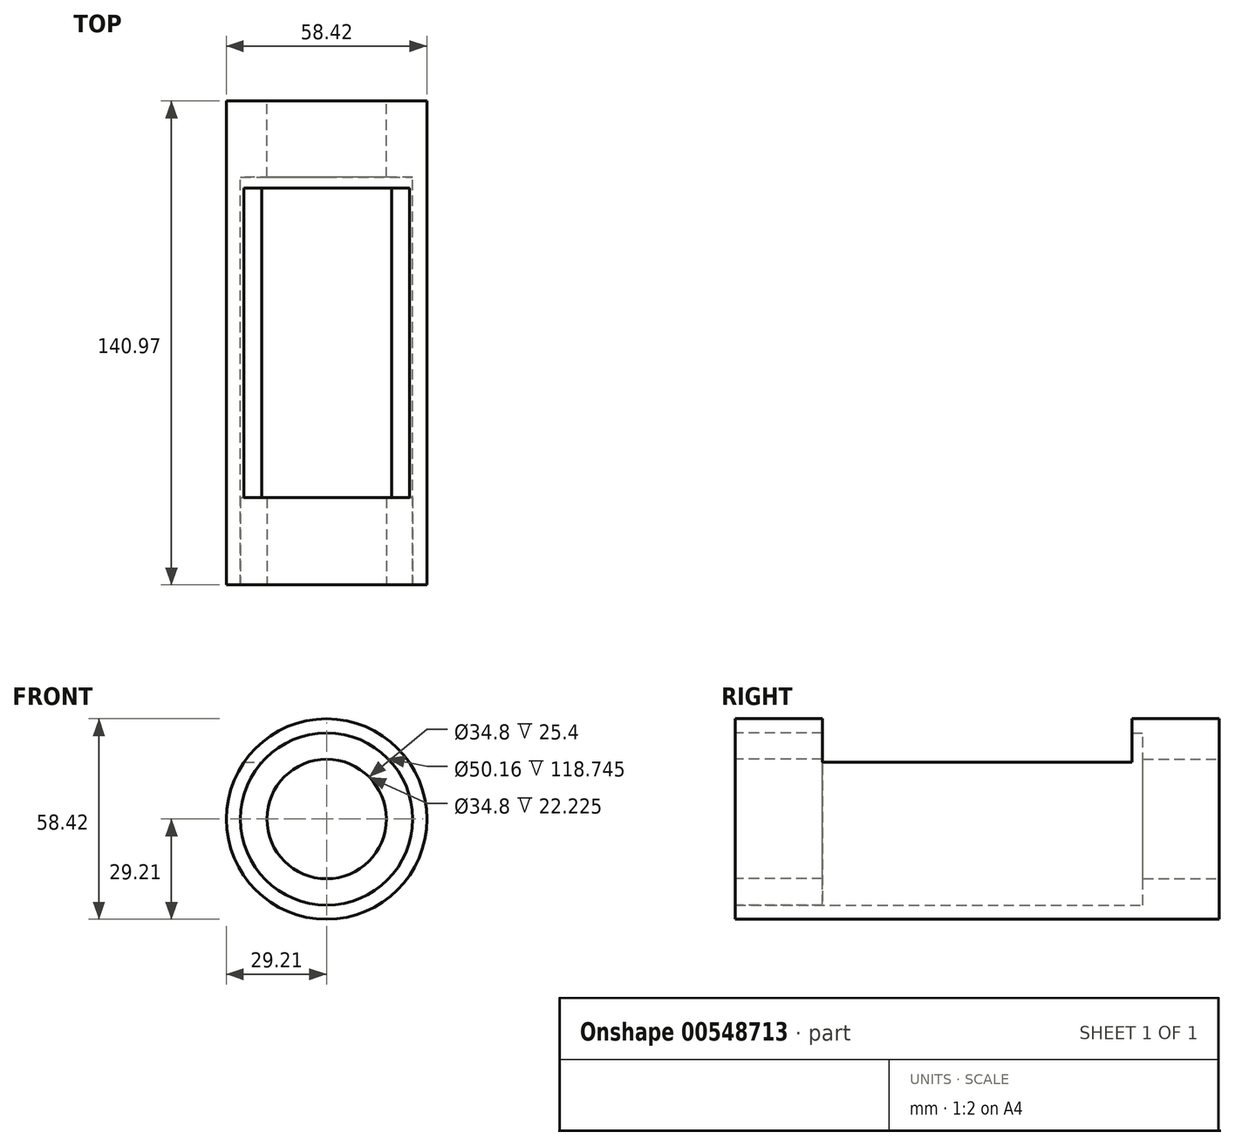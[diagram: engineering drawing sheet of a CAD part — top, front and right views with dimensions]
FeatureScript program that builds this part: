
annotation { "Feature Type Name" : "Feature", "Feature Type Description" : "" }
export const myFeature = defineFeature(function(context is Context, id is Id, definition is map)
    precondition{}
    {
        {
            var Q0;
            Q0=qCreatedBy(makeId("Front.planeOp"),FACE);
            var sketch = newSketch(context, id + "F0", { "sketchPlane" : qUnion([Q0])});
            skCircle(sketch, "E0", {"center": v(0, 0) * mm, "radius": 29.21 * mm});
            skCircle(sketch, "E1", {"center": v(0, 0) * mm, "radius": 25.08 * mm});
            skCircle(sketch, "E2", {"center": v(0, 0) * mm, "radius": 17.4 * mm});
            skPoint(sketch, "E3", {"position": v(0, 29.21) * mm});
            skLineSegment(sketch, "E4", {"start": v(0, 29.21) * mm, "end": v(0, 0) * mm, "construction": true});
            skLineSegment(sketch, "E5", {"start": v(-11.91, 26.67) * mm, "end": v(11.91, 26.67) * mm});
            skLineSegment(sketch, "E6", {"start": v(-15.1, 29.21) * mm, "end": v(32.37, 29.2) * mm, "construction": true});
            skLineSegment(sketch, "E7", {"start": v(0, -1) * mm, "end": v(0, -29.21) * mm, "construction": true});
            skSolve(sketch);
        }
        {
            var Q0;
            Q0=makeQuery(id+"F0.imprint","IMPRINT",FACE,{"disambiguationData":[TD([[makeQuery(id+"F0.imprint","IMPRINT",EDGE,{"derivedFrom":sQuery(id+"F0.wireOp",EDGE,"E1")}),1.0]])]});
            extrude(context, id + "F1", {"entities" : qUnion([Q0]), "depth" : 22.22 * mm, "offsetDistance" : 25.4 * mm});
        }
        {
            var Q0;
            Q0 = qSketchRegion(id + "F0", true);
            extrude(context, id + "F2", {"entities" : qUnion([Q0]), "operationType" : NewBodyOperationType.ADD, "depth" : 140.97 * mm, "offsetDistance" : 25.4 * mm});
        }
        {
            var Q0;
            Q0=qCreatedBy(makeId("Right.planeOp"),FACE);
            var sketch = newSketch(context, id + "F3", { "sketchPlane" : qUnion([Q0])});
            skLineSegment(sketch, "E8", {"start": v(0, 29.21) * mm, "end": v(-167.52, 29.2) * mm, "construction": true});
            skLineSegment(sketch, "E9.bottom", {"start": v(-25.4, 29.2) * mm, "end": v(-115.57, 29.2) * mm});
            skLineSegment(sketch, "E9.top", {"start": v(-25.4, 16.5) * mm, "end": v(-115.57, 16.5) * mm});
            skLineSegment(sketch, "E9.left", {"start": v(-25.4, 29.2) * mm, "end": v(-25.4, 16.5) * mm});
            skLineSegment(sketch, "E9.right", {"start": v(-115.57, 29.2) * mm, "end": v(-115.57, 16.5) * mm});
            skLineSegment(sketch, "E10", {"start": v(0, -29.21) * mm, "end": v(-167.52, -29.21) * mm, "construction": true});
            skSolve(sketch);
        }
        {
            var Q0;
            Q0 = qSketchRegion(id + "F3", true);
            extrude(context, id + "F4", {"entities" : qUnion([Q0]), "operationType" : NewBodyOperationType.REMOVE, "endBound" : BoundingType.SYMMETRIC, "oppositeDirection" : true, "depth" : 76.2 * mm, "offsetDistance" : 25.4 * mm});
        }
        {
            var Q0;
            Q0=makeQuery(id+"F2.opExtrude","CAP_FACE",FACE,{"disambiguationData":[OSD([sQuery(id+"F0.wireOp",EDGE,"E0"),sQuery(id+"F0.wireOp",EDGE,"E1")])],"isStart":false});
            var sketch = newSketch(context, id + "F5", { "sketchPlane" : qUnion([Q0])});
            skCircle(sketch, "E11", {"center": v(0, 0) * mm, "radius": 17.4 * mm});
            skPoint(sketch, "E12", {"position": v(-29.21, 0) * mm});
            skSolve(sketch);
        }
        {
            var Q0;
            Q0=makeQuery(id+"F5.imprint","IMPRINT",FACE,{"disambiguationData":[TD([[makeQuery(id+"F5.imprint","IMPRINT",EDGE,{"derivedFrom":sQuery(id+"F5.wireOp",EDGE,"E11")}),-1.0]])]});
            extrude(context, id + "F6", {"entities" : qUnion([Q0]), "oppositeDirection" : true, "depth" : 25.4 * mm, "offsetDistance" : 25.4 * mm});
        }
        {
            var Q0;
            Q0=makeQuery(id+"F6.opExtrude","CAP_FACE",FACE,{"disambiguationData":[OSD([sQuery(id+"F0.wireOp",EDGE,"E1"),sQuery(id+"F5.wireOp",EDGE,"E11")])],"isStart":false});
            cPlane(context, id + "F7", {"entities" : qUnion([Q0]), "cplaneType" : CPlaneType.OFFSET, "offset" : 9.52 * mm, "width" : 152.4 * mm, "height" : 152.4 * mm});
        }
    });
